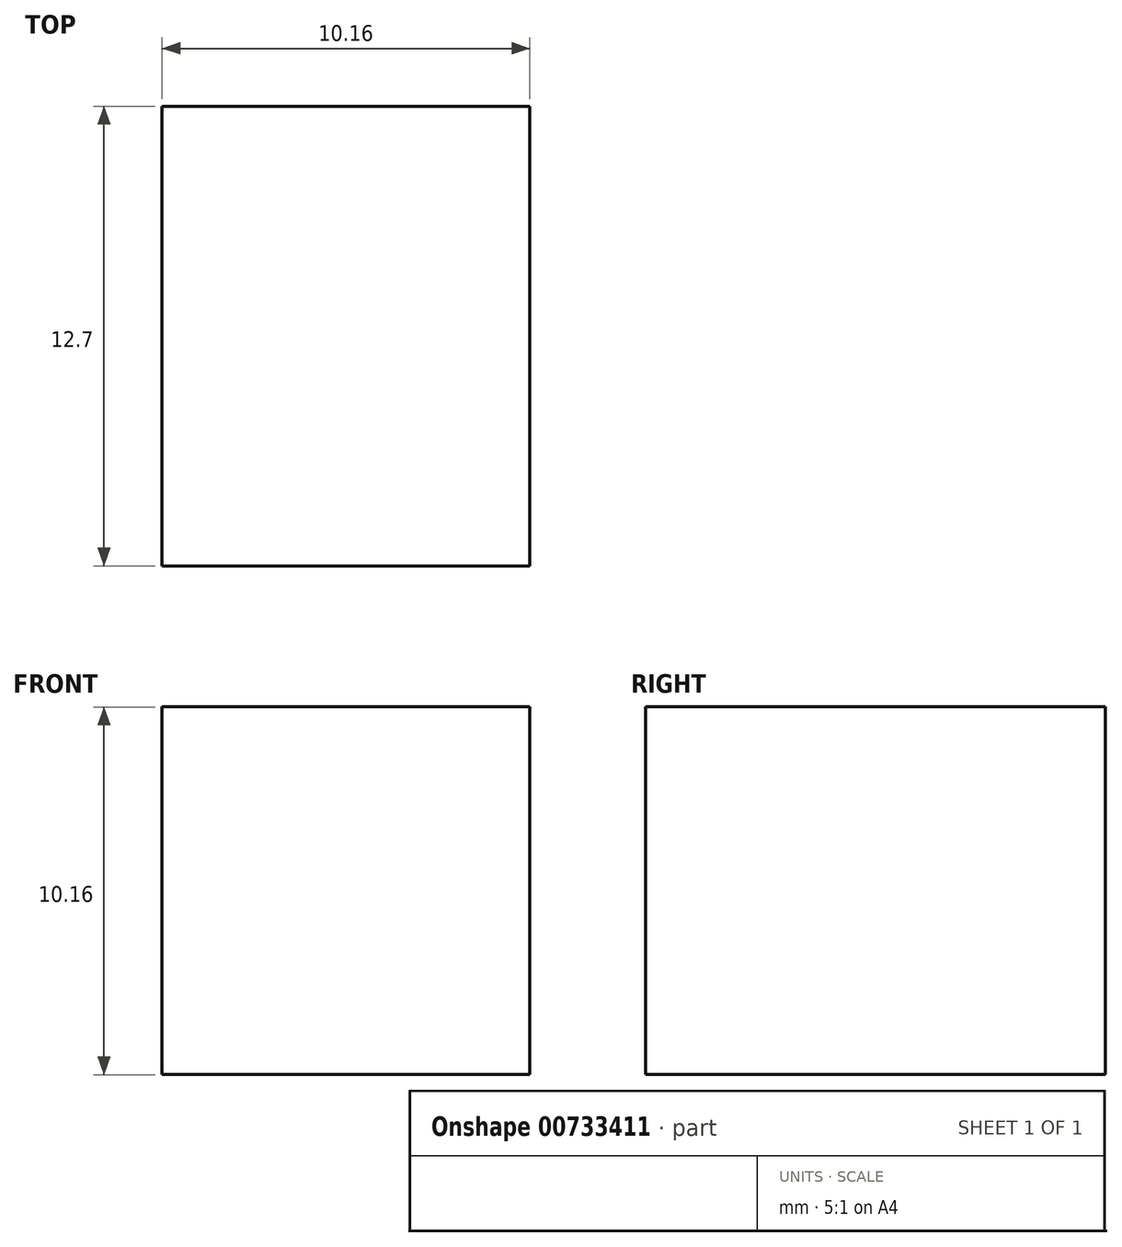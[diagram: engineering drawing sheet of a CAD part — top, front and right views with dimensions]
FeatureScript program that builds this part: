
annotation { "Feature Type Name" : "Feature", "Feature Type Description" : "" }
export const myFeature = defineFeature(function(context is Context, id is Id, definition is map)
    precondition{}
    {
        {
            var Q0;
            Q0=qCreatedBy(makeId("Front.planeOp"),FACE);
            var sketch = newSketch(context, id + "F0", { "sketchPlane" : qUnion([Q0])});
            skLineSegment(sketch, "E0.bottom", {"start": v(-2.21, 3.51) * mm, "end": v(7.95, 3.51) * mm});
            skLineSegment(sketch, "E0.top", {"start": v(-2.21, -6.65) * mm, "end": v(7.95, -6.65) * mm});
            skLineSegment(sketch, "E0.left", {"start": v(-2.21, 3.51) * mm, "end": v(-2.21, -6.65) * mm});
            skLineSegment(sketch, "E0.right", {"start": v(7.95, 3.51) * mm, "end": v(7.95, -6.65) * mm});
            skSolve(sketch);
        }
        {
            var Q0;
            Q0 = qSketchRegion(id + "F0", true);
            extrude(context, id + "F1", {"entities" : qUnion([Q0]), "depth" : 12.7 * mm, "offsetDistance" : 25.4 * mm});
        }
    });
